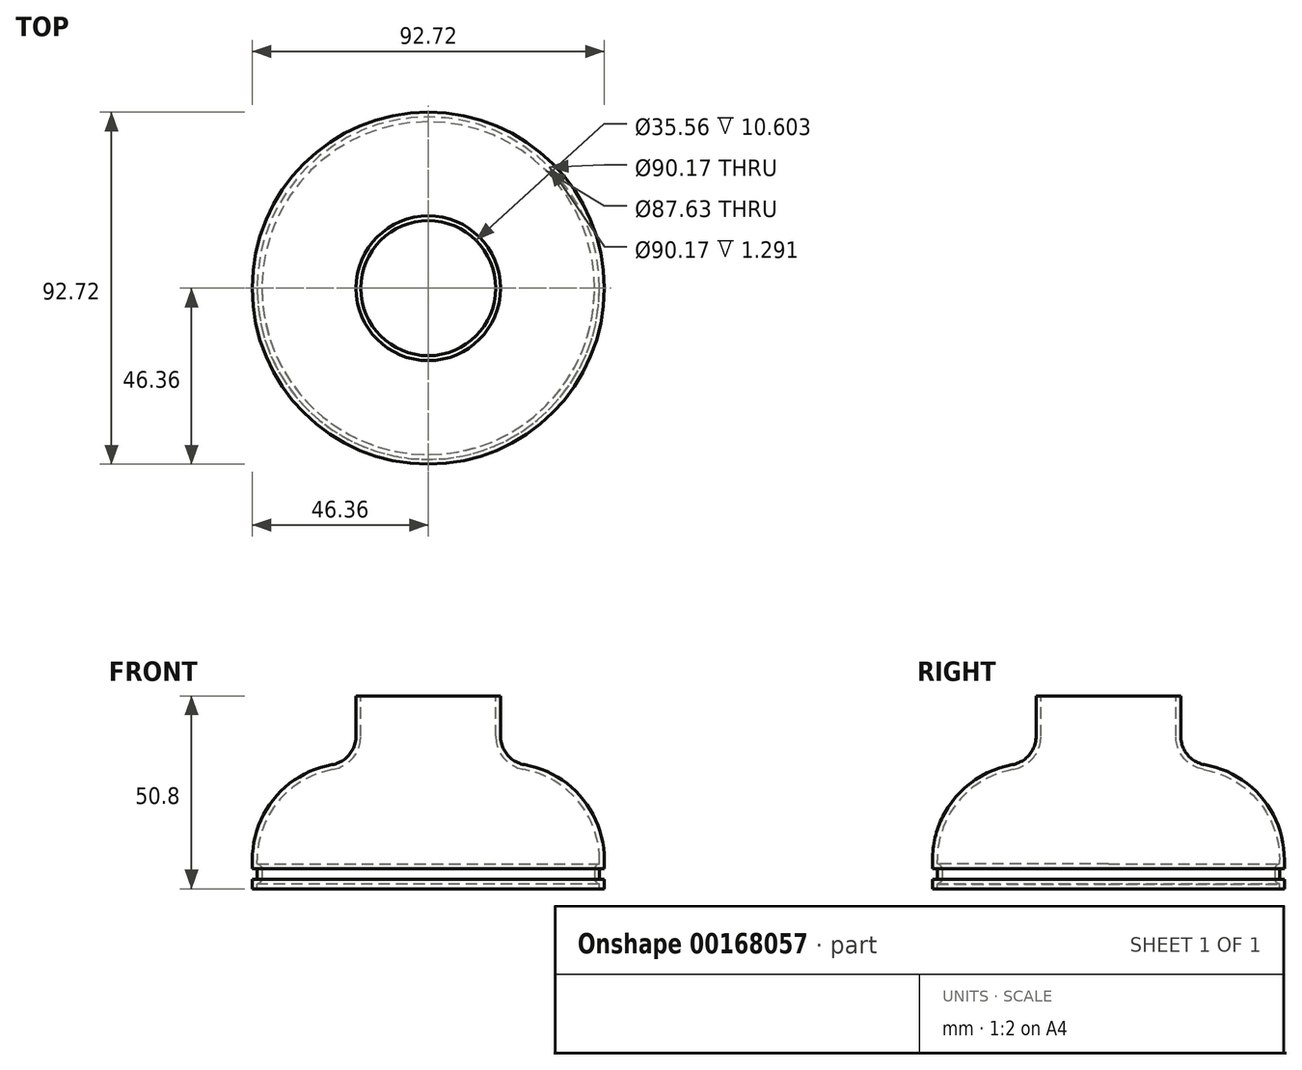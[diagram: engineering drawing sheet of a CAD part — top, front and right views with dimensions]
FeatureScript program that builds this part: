
annotation { "Feature Type Name" : "Feature", "Feature Type Description" : "" }
export const myFeature = defineFeature(function(context is Context, id is Id, definition is map)
    precondition{}
    {
        {
            var Q0;
            Q0=qCreatedBy(makeId("Front.planeOp"),FACE);
            var sketch = newSketch(context, id + "F0", { "sketchPlane" : qUnion([Q0])});
            skLineSegment(sketch, "E0", {"start": v(0, 0) * mm, "end": v(46.35, 0) * mm});
            skLineSegment(sketch, "E1", {"start": v(46.35, 0) * mm, "end": v(46.35, 7.62) * mm});
            skLineSegment(sketch, "E2", {"start": v(19.05, 33.02) * mm, "end": v(19.05, 50.8) * mm});
            skLineSegment(sketch, "E3", {"start": v(19.05, 50.8) * mm, "end": v(0, 50.8) * mm});
            skLineSegment(sketch, "E4", {"start": v(0, 50.8) * mm, "end": v(0, 0) * mm});
            skArc(sketch, "E5", {"start": v(46.35, 7.62) * mm, "mid": v(38.23, 26.27) * mm, "end": v(19.05, 33.02) * mm});
            skSolve(sketch);
        }
        {
            var Q0;
            Q0=makeQuery(id+"F0.imprint","IMPRINT",FACE,{"disambiguationData":[TD([[makeQuery(id+"F0.imprint","IMPRINT",EDGE,{"derivedFrom":sQuery(id+"F0.wireOp",EDGE,"E0")}),1.0]])]});
            var Q1;
            Q1=sQuery(id+"F0.wireOp",EDGE,"E4");
            revolve(context, id + "F1", {"entities" : qUnion([Q0]), "axis" : qUnion([Q1]), "revolveType" : RevolveType.FULL});
        }
        {
            var Q0;
            Q0=makeQuery(id+"F1.opRevolve","SWEPT_EDGE",EDGE,{"disambiguationData":[OSD([sQuery(id+"F0.wireOp",EDGE,"E2"),sQuery(id+"F0.wireOp",EDGE,"E5")])]});
            fillet(context, id + "F2", {"entities" : qUnion([Q0]), "radius" : 7.62 * mm, "tangentPropagation" : true, "allowEdgeOverflow" : false});
        }
        {
            var Q0;
            Q0=qCreatedBy(makeId("Front.planeOp"),FACE);
            var sketch = newSketch(context, id + "F3", { "sketchPlane" : qUnion([Q0])});
            skArc(sketch, "E6", {"start": v(38.23, 26.27) * mm, "mid": v(32.27, 39.18) * mm, "end": v(19.05, 44.45) * mm});
            skLineSegment(sketch, "E7", {"start": v(19.05, 44.45) * mm, "end": v(0, 44.45) * mm});
            skLineSegment(sketch, "E8", {"start": v(39.64, 0) * mm, "end": v(38.23, 26.27) * mm});
            skSolve(sketch);
        }
        {
            var Q0;
            Q0=qCreatedBy(makeId("Front.planeOp"),FACE);
            var sketch = newSketch(context, id + "F4", { "sketchPlane" : qUnion([Q0])});
            skLineSegment(sketch, "E9.bottom", {"start": v(46.35, 2.54) * mm, "end": v(45.09, 2.54) * mm});
            skLineSegment(sketch, "E9.top", {"start": v(46.35, 5.33) * mm, "end": v(45.09, 5.33) * mm});
            skLineSegment(sketch, "E9.left", {"start": v(46.35, 2.54) * mm, "end": v(46.35, 5.33) * mm});
            skLineSegment(sketch, "E9.right", {"start": v(45.09, 2.54) * mm, "end": v(45.09, 5.33) * mm});
            skSolve(sketch);
        }
        {
            var Q0;
            Q0 = qSketchRegion(id + "F4", true);
            var Q1;
            Q1=sQuery(id+"F0.wireOp",EDGE,"E4");
            revolve(context, id + "F5", {"operationType" : NewBodyOperationType.REMOVE, "entities" : qUnion([Q0]), "axis" : qUnion([Q1]), "revolveType" : RevolveType.FULL, "oppositeDirection" : true});
        }
        {
            var Q0;
            Q0=makeQuery(id+"F5.boolean.opBoolean","COPY",FACE,{"derivedFrom":makeQuery(id+"F5.opRevolve","SWEPT_FACE",FACE,{"disambiguationData":[OSD([sQuery(id+"F4.wireOp",EDGE,"E9.right")])]})});
            fillet(context, id + "F6", {"entities" : qUnion([Q0]), "radius" : 0.25 * mm, "tangentPropagation" : true, "allowEdgeOverflow" : false});
        }
        {
            var Q0;
            Q0=makeQuery(id+"F1.opRevolve","SWEPT_FACE",FACE,{"disambiguationData":[OSD([sQuery(id+"F0.wireOp",EDGE,"E0")])]});
            var Q1;
            Q1=makeQuery(id+"F1.opRevolve","SWEPT_FACE",FACE,{"disambiguationData":[OSD([sQuery(id+"F0.wireOp",EDGE,"E3")])]});
            shell(context, id + "F7", {"entities" : qUnion([Q0, Q1]), "thickness" : 1.27 * mm});
        }
    });
